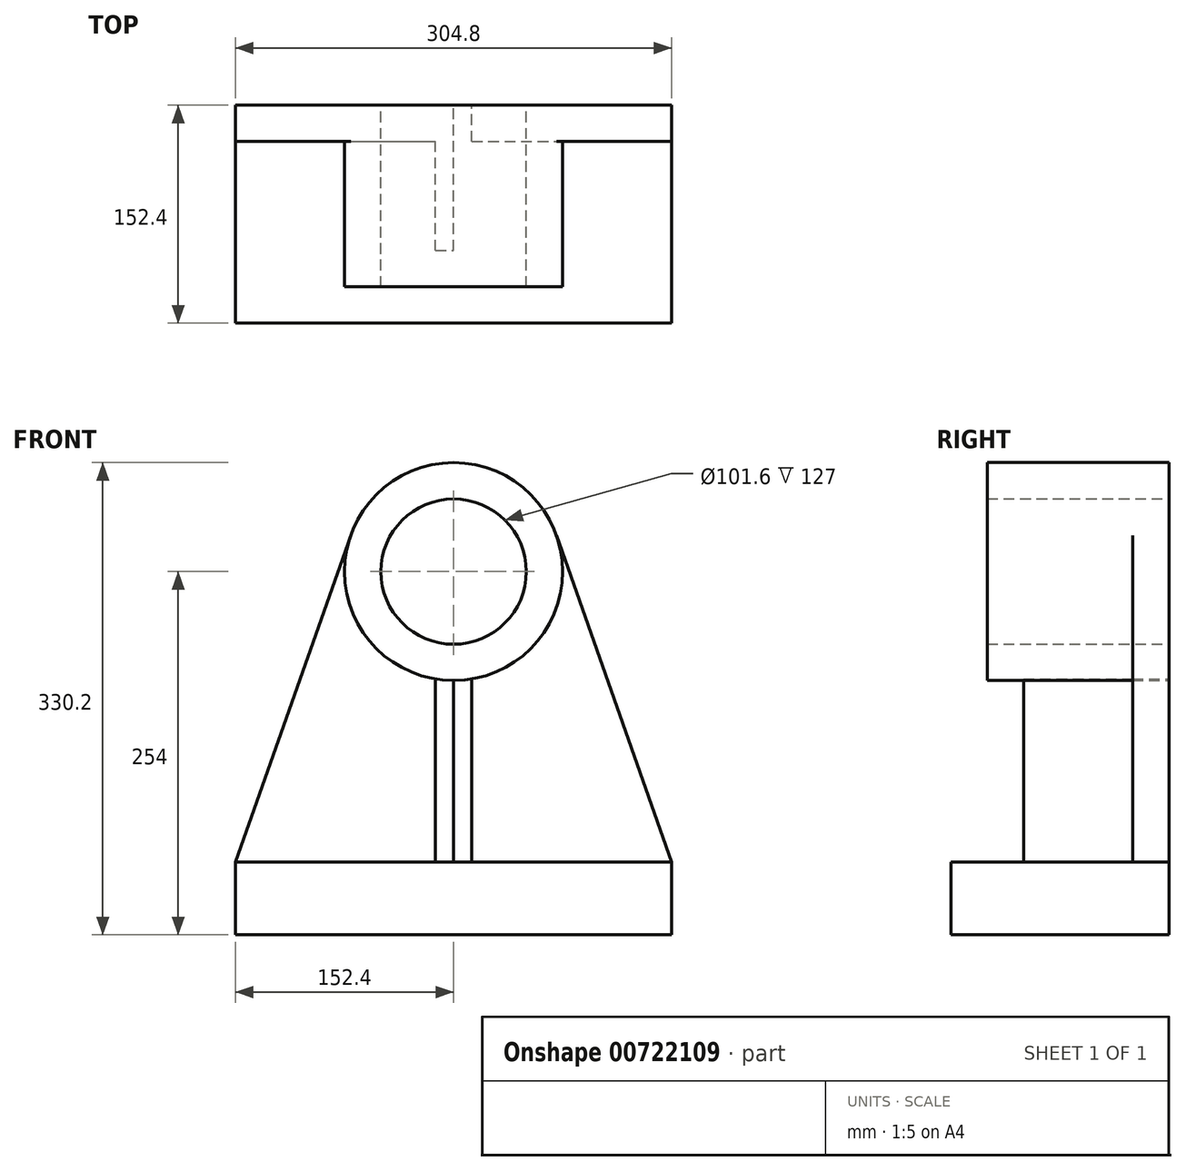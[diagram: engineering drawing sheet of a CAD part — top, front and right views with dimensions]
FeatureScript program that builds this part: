
annotation { "Feature Type Name" : "Feature", "Feature Type Description" : "" }
export const myFeature = defineFeature(function(context is Context, id is Id, definition is map)
    precondition{}
    {
        {
            var Q0;
            Q0=qCreatedBy(makeId("Front.planeOp"),FACE);
            var sketch = newSketch(context, id + "F0", { "sketchPlane" : qUnion([Q0])});
            skLineSegment(sketch, "E0.bottom", {"start": v(0, 0) * mm, "end": v(304.8, 0) * mm});
            skLineSegment(sketch, "E0.top", {"start": v(0, 50.8) * mm, "end": v(304.8, 50.8) * mm});
            skLineSegment(sketch, "E0.left", {"start": v(0, 0) * mm, "end": v(0, 50.8) * mm});
            skLineSegment(sketch, "E0.right", {"start": v(304.8, 0) * mm, "end": v(304.8, 50.8) * mm});
            skLineSegment(sketch, "E1.top", {"start": v(0, 254) * mm, "end": v(304.8, 254) * mm});
            skLineSegment(sketch, "E1.left", {"start": v(0, 0) * mm, "end": v(0, 254) * mm});
            skLineSegment(sketch, "E1.right", {"start": v(304.8, 0) * mm, "end": v(304.8, 254) * mm});
            skCircle(sketch, "E2", {"center": v(152.4, 254) * mm, "radius": 76.2 * mm});
            skCircle(sketch, "E3", {"center": v(152.4, 254) * mm, "radius": 50.8 * mm});
            skLineSegment(sketch, "E4", {"start": v(0, 50.8) * mm, "end": v(80.53, 279.33) * mm});
            skLineSegment(sketch, "E5", {"start": v(304.8, 50.8) * mm, "end": v(224.27, 279.33) * mm});
            skLineSegment(sketch, "E6", {"start": v(152.4, 50.8) * mm, "end": v(152.4, 177.8) * mm});
            skLineSegment(sketch, "E7.bottom", {"start": v(152.4, 50.8) * mm, "end": v(165.1, 50.8) * mm});
            skLineSegment(sketch, "E7.top", {"start": v(152.4, 178.87) * mm, "end": v(165.1, 178.87) * mm});
            skLineSegment(sketch, "E7.left", {"start": v(152.4, 50.8) * mm, "end": v(152.4, 178.87) * mm});
            skLineSegment(sketch, "E7.right", {"start": v(165.1, 50.8) * mm, "end": v(165.1, 178.87) * mm});
            skLineSegment(sketch, "E8.MirrorCS", {"start": v(139.7, 50.8) * mm, "end": v(139.7, 178.87) * mm});
            skLineSegment(sketch, "E9.MirrorCS", {"start": v(152.4, 178.87) * mm, "end": v(139.7, 178.87) * mm});
            skSolve(sketch);
        }
        {
            var Q0;
            {var subQ0=sQuery(id+"F0.wireOp",EDGE,"E0.bottom");Q0=makeQuery(id+"F0.imprint","IMPRINT",FACE,{"disambiguationData":[TD([[makeQuery(id+"F0.imprint","IMPRINT",EDGE,{"derivedFrom":subQ0}),1.0]])]});}
            extrude(context, id + "F1", {"entities" : qUnion([Q0]), "depth" : 152.4 * mm, "offsetDistance" : 25.4 * mm});
        }
        {
            var Q0;
            {var subQ5=sQuery(id+"F0.wireOp",EDGE,"E7.right");Q0=makeQuery(id+"F0.imprint","IMPRINT",FACE,{"disambiguationData":[TD([[makeQuery(id+"F0.imprint","IMPRINT",EDGE,{"derivedFrom":subQ5}),-1.0]])]});}
            var Q1;
            {var subQ5=sQuery(id+"F0.wireOp",EDGE,"E8.MirrorCS");Q1=makeQuery(id+"F0.imprint","IMPRINT",FACE,{"disambiguationData":[TD([[makeQuery(id+"F0.imprint","IMPRINT",EDGE,{"derivedFrom":subQ5}),1.0]])]});}
            var Q2;
            {var subQ0=sQuery(id+"F0.wireOp",EDGE,"E4");var subQ1=sQuery(id+"F0.wireOp",EDGE,"E1.top");var subQ2=makeQuery(id+"F0.imprint","INTERSECT",VERTEX,{"derivedFrom":[subQ1,subQ0]});Q2=makeQuery(id+"F0.imprint","IMPRINT",FACE,{"disambiguationData":[TD([[makeQuery(id+"F0.imprint","IMPRINT",EDGE,{"disambiguationData":[TD([[subQ2,-1.0]])],"derivedFrom":subQ1}),1.0]])]});}
            var Q3;
            {var subQ0=sQuery(id+"F0.wireOp",EDGE,"E5");var subQ1=sQuery(id+"F0.wireOp",EDGE,"E1.top");var subQ2=makeQuery(id+"F0.imprint","INTERSECT",VERTEX,{"derivedFrom":[subQ1,subQ0]});Q3=makeQuery(id+"F0.imprint","IMPRINT",FACE,{"disambiguationData":[TD([[makeQuery(id+"F0.imprint","IMPRINT",EDGE,{"disambiguationData":[TD([[subQ2,1.0]])],"derivedFrom":subQ1}),1.0]])]});}
            extrude(context, id + "F2", {"entities" : qUnion([Q0, Q1, Q2, Q3]), "operationType" : NewBodyOperationType.ADD, "depth" : 25.4 * mm, "offsetDistance" : 25.4 * mm});
        }
        {
            var Q0;
            {var subQ4=sQuery(id+"F0.wireOp",EDGE,"E7.bottom");Q0=makeQuery(id+"F0.imprint","IMPRINT",FACE,{"disambiguationData":[TD([[makeQuery(id+"F0.imprint","IMPRINT",EDGE,{"derivedFrom":subQ4}),1.0]])]});}
            var Q1;
            {var subQ3=sQuery(id+"F0.wireOp",EDGE,"E8.MirrorCS");Q1=makeQuery(id+"F0.imprint","IMPRINT",FACE,{"disambiguationData":[TD([[makeQuery(id+"F0.imprint","IMPRINT",EDGE,{"derivedFrom":subQ3}),-1.0]])]});}
            extrude(context, id + "F3", {"entities" : qUnion([Q0, Q1]), "operationType" : NewBodyOperationType.ADD, "depth" : 101.6 * mm, "offsetDistance" : 25.4 * mm});
        }
        {
            var Q0;
            {var subQ4=sQuery(id+"F0.wireOp",EDGE,"E7.top");Q0=makeQuery(id+"F0.imprint","IMPRINT",FACE,{"disambiguationData":[TD([[makeQuery(id+"F0.imprint","IMPRINT",EDGE,{"derivedFrom":subQ4}),1.0]])]});}
            var Q1;
            {var subQ0=sQuery(id+"F0.wireOp",EDGE,"E2");var subQ2=sQuery(id+"F0.wireOp",EDGE,"E1.top");var subQ7=makeQuery(id+"F0.imprint","INTERSECT",VERTEX,{"disambiguationData":[OD(0.0)],"derivedFrom":[subQ2,subQ0]});Q1=makeQuery(id+"F0.imprint","IMPRINT",FACE,{"disambiguationData":[TD([[makeQuery(id+"F0.imprint","IMPRINT",EDGE,{"disambiguationData":[TD([[subQ7,-1.0]])],"derivedFrom":subQ2}),1.0]])]});}
            var Q2;
            {var subQ0=sQuery(id+"F0.wireOp",EDGE,"E9.MirrorCS");Q2=makeQuery(id+"F0.imprint","IMPRINT",FACE,{"disambiguationData":[TD([[makeQuery(id+"F0.imprint","IMPRINT",EDGE,{"derivedFrom":subQ0}),1.0]])]});}
            var Q3;
            {var subQ0=sQuery(id+"F0.wireOp",EDGE,"E7.top");Q3=makeQuery(id+"F0.imprint","IMPRINT",FACE,{"disambiguationData":[TD([[makeQuery(id+"F0.imprint","IMPRINT",EDGE,{"derivedFrom":subQ0}),-1.0]])]});}
            extrude(context, id + "F4", {"entities" : qUnion([Q0, Q1, Q2, Q3]), "operationType" : NewBodyOperationType.ADD, "depth" : 127 * mm, "offsetDistance" : 25.4 * mm});
        }
    });
